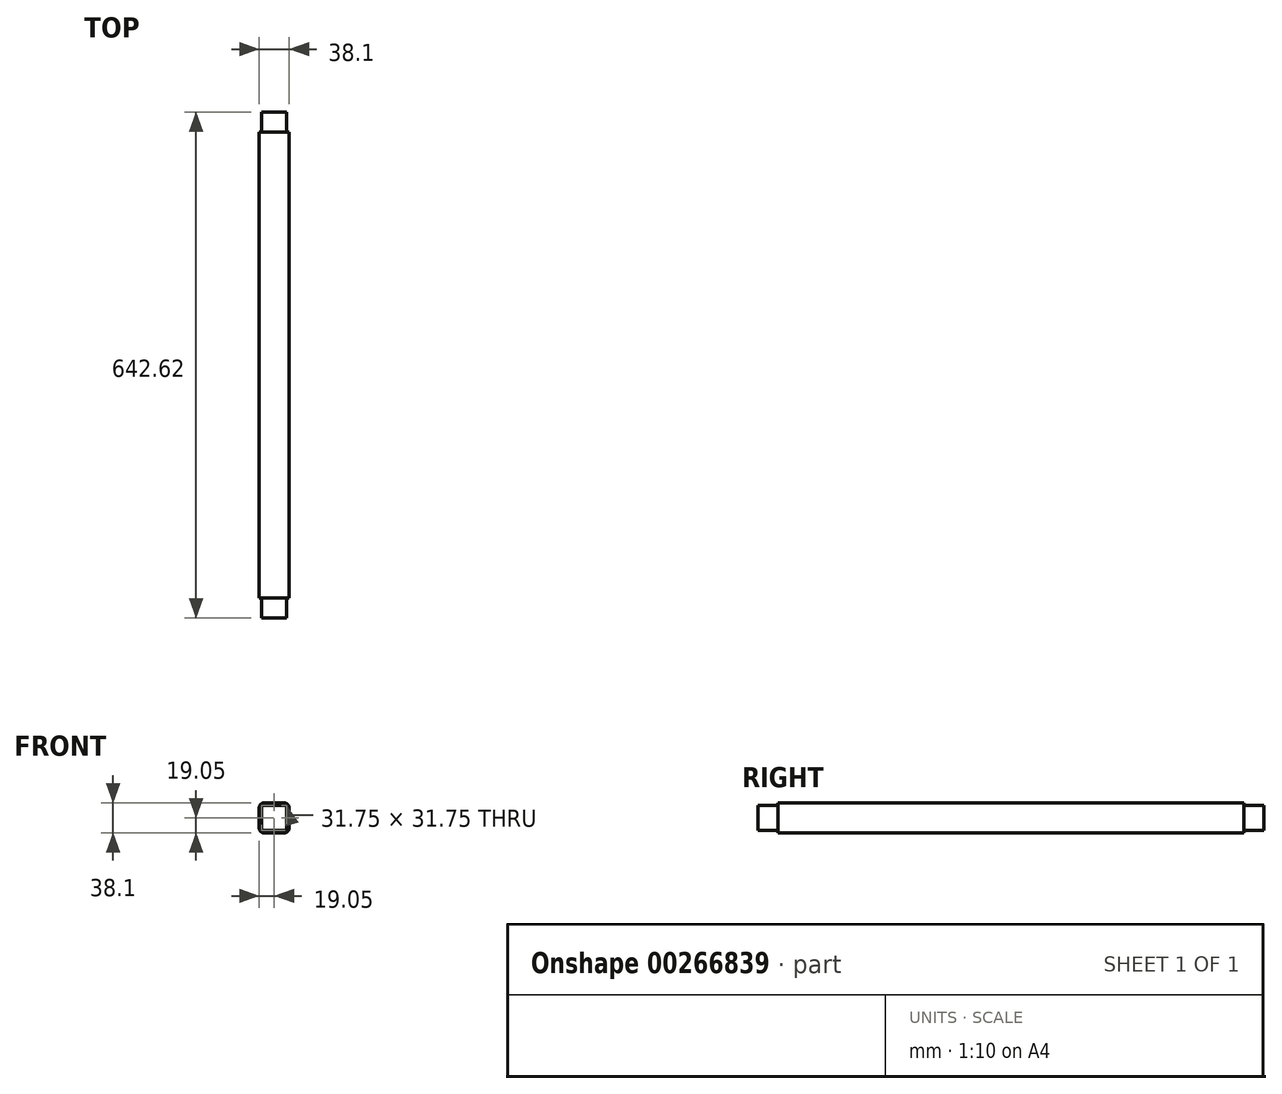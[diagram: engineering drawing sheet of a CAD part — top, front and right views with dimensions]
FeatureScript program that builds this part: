
annotation { "Feature Type Name" : "Feature", "Feature Type Description" : "" }
export const myFeature = defineFeature(function(context is Context, id is Id, definition is map)
    precondition{}
    {
        {
            var Q0;
            Q0=qCreatedBy(makeId("Front.planeOp"),FACE);
            var sketch = newSketch(context, id + "F0", { "sketchPlane" : qUnion([Q0])});
            skLineSegment(sketch, "E0.bottom", {"start": v(-19.05, -19.05) * mm, "end": v(19.05, -19.05) * mm});
            skLineSegment(sketch, "E0.top", {"start": v(-19.05, 19.05) * mm, "end": v(19.05, 19.05) * mm});
            skLineSegment(sketch, "E0.left", {"start": v(-19.05, -19.05) * mm, "end": v(-19.05, 19.05) * mm});
            skLineSegment(sketch, "E0.right", {"start": v(19.05, -19.05) * mm, "end": v(19.05, 19.05) * mm});
            skPoint(sketch, "E0.middle", {"position": v(0, 0) * mm});
            skSolve(sketch);
        }
        {
            var Q0;
            Q0 = qSketchRegion(id + "F0", true);
            extrude(context, id + "F1", {"entities" : qUnion([Q0]), "endBound" : BoundingType.SYMMETRIC, "depth" : 591.82 * mm});
        }
        {
            var Q0;
            Q0=makeQuery(id+"F1.opExtrude","CAP_FACE",FACE,{"disambiguationData":[OSD([sQuery(id+"F0.wireOp",EDGE,"E0.bottom"),sQuery(id+"F0.wireOp",EDGE,"E0.top"),sQuery(id+"F0.wireOp",EDGE,"E0.left"),sQuery(id+"F0.wireOp",EDGE,"E0.right")])],"isStart":false});
            var sketch = newSketch(context, id + "F2", { "sketchPlane" : qUnion([Q0])});
            skLineSegment(sketch, "E1.bottom", {"start": v(-15.87, 15.88) * mm, "end": v(15.88, 15.88) * mm});
            skLineSegment(sketch, "E1.top", {"start": v(-15.88, -15.88) * mm, "end": v(15.88, -15.88) * mm});
            skLineSegment(sketch, "E1.left", {"start": v(-15.87, 15.88) * mm, "end": v(-15.88, -15.88) * mm});
            skLineSegment(sketch, "E1.right", {"start": v(15.88, 15.88) * mm, "end": v(15.87, -15.88) * mm});
            skPoint(sketch, "E1.middle", {"position": v(0, 0) * mm});
            skSolve(sketch);
        }
        {
            var Q0;
            Q0 = qSketchRegion(id + "F2", true);
            extrude(context, id + "F3", {"entities" : qUnion([Q0]), "operationType" : NewBodyOperationType.ADD, "depth" : 25.4 * mm});
        }
        {
            var Q0;
            Q0=makeQuery(id+"F1.opExtrude","CAP_FACE",FACE,{"disambiguationData":[OSD([sQuery(id+"F0.wireOp",EDGE,"E0.bottom"),sQuery(id+"F0.wireOp",EDGE,"E0.top"),sQuery(id+"F0.wireOp",EDGE,"E0.left"),sQuery(id+"F0.wireOp",EDGE,"E0.right")])],"isStart":true});
            var sketch = newSketch(context, id + "F4", { "sketchPlane" : qUnion([Q0])});
            skLineSegment(sketch, "E2.bottom", {"start": v(-15.88, -15.88) * mm, "end": v(15.88, -15.88) * mm});
            skLineSegment(sketch, "E2.top", {"start": v(-15.88, 15.88) * mm, "end": v(15.88, 15.88) * mm});
            skLineSegment(sketch, "E2.left", {"start": v(-15.88, -15.88) * mm, "end": v(-15.88, 15.88) * mm});
            skLineSegment(sketch, "E2.right", {"start": v(15.88, -15.88) * mm, "end": v(15.88, 15.88) * mm});
            skPoint(sketch, "E2.middle", {"position": v(0, 0) * mm});
            skSolve(sketch);
        }
        {
            var Q0;
            Q0 = qSketchRegion(id + "F4", true);
            extrude(context, id + "F5", {"entities" : qUnion([Q0]), "operationType" : NewBodyOperationType.ADD, "depth" : 25.4 * mm});
        }
        {
            var Q0;
            Q0=makeQuery(id+"F1.opExtrude","SWEPT_EDGE",EDGE,{"disambiguationData":[OSD([sQuery(id+"F0.wireOp",EDGE,"E0.top"),sQuery(id+"F0.wireOp",EDGE,"E0.right")])]});
            var Q1;
            Q1=makeQuery(id+"F1.opExtrude","SWEPT_EDGE",EDGE,{"disambiguationData":[OSD([sQuery(id+"F0.wireOp",EDGE,"E0.bottom"),sQuery(id+"F0.wireOp",EDGE,"E0.right")])]});
            var Q2;
            Q2=makeQuery(id+"F1.opExtrude","SWEPT_EDGE",EDGE,{"disambiguationData":[OSD([sQuery(id+"F0.wireOp",EDGE,"E0.bottom"),sQuery(id+"F0.wireOp",EDGE,"E0.left")])]});
            var Q3;
            Q3=makeQuery(id+"F1.opExtrude","SWEPT_EDGE",EDGE,{"disambiguationData":[OSD([sQuery(id+"F0.wireOp",EDGE,"E0.top"),sQuery(id+"F0.wireOp",EDGE,"E0.left")])]});
            fillet(context, id + "F6", {"entities" : qUnion([Q0, Q1, Q2, Q3]), "radius" : 6.35 * mm, "tangentPropagation" : true, "allowEdgeOverflow" : false});
        }
    });
